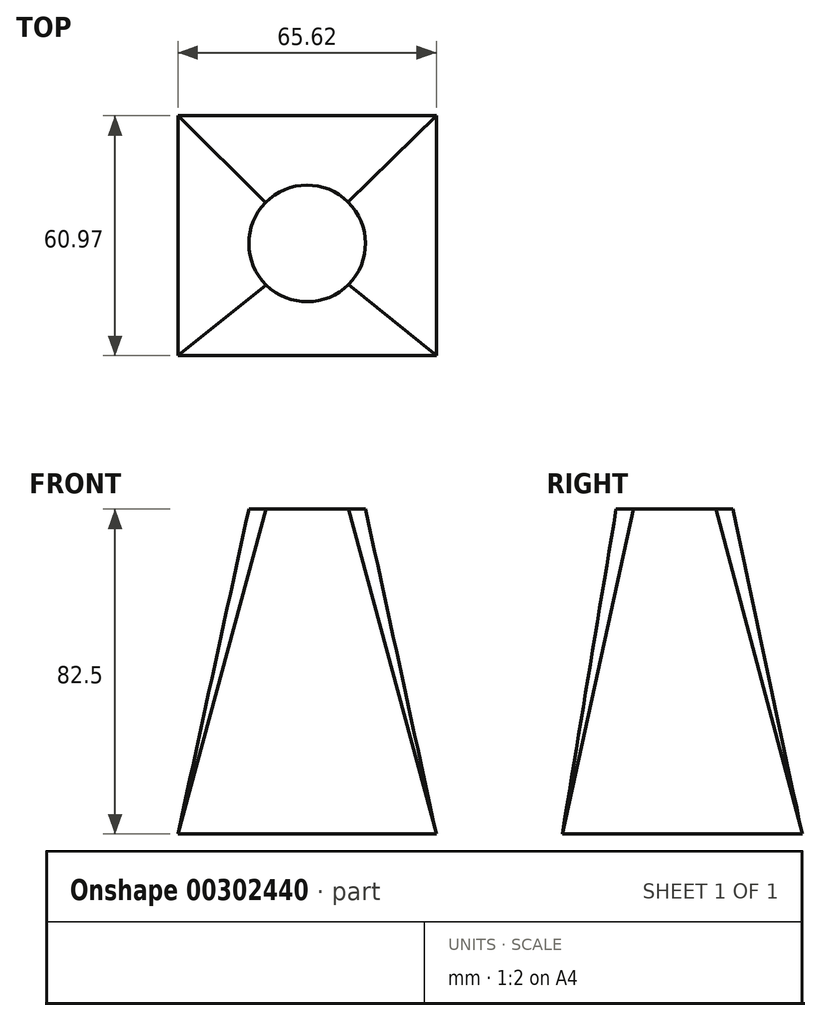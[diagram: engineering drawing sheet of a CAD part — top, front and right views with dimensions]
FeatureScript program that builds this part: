
annotation { "Feature Type Name" : "Feature", "Feature Type Description" : "" }
export const myFeature = defineFeature(function(context is Context, id is Id, definition is map)
    precondition{}
    {
        {
            var Q0;
            Q0=qCreatedBy(makeId("Top.planeOp"),FACE);
            var sketch = newSketch(context, id + "F0", { "sketchPlane" : qUnion([Q0])});
            skLineSegment(sketch, "E0.bottom", {"start": v(-32.81, 32.47) * mm, "end": v(32.81, 32.47) * mm});
            skLineSegment(sketch, "E0.top", {"start": v(-32.81, -28.5) * mm, "end": v(32.81, -28.5) * mm});
            skLineSegment(sketch, "E0.left", {"start": v(-32.81, 32.47) * mm, "end": v(-32.81, -28.5) * mm});
            skLineSegment(sketch, "E0.right", {"start": v(32.81, 32.47) * mm, "end": v(32.81, -28.5) * mm});
            skSolve(sketch);
        }
        {
            var Q0;
            Q0=makeQuery(id+"F0.imprint","IMPRINT",FACE,{"disambiguationData":[TD([[makeQuery(id+"F0.imprint","IMPRINT",EDGE,{"derivedFrom":sQuery(id+"F0.wireOp",EDGE,"E0.bottom")}),-1.0]])]});
            cPlane(context, id + "F1", {"entities" : qUnion([Q0]), "cplaneType" : CPlaneType.OFFSET, "offset" : 82.5 * mm, "width" : 150 * mm, "height" : 150 * mm});
        }
        {
            var Q0;
            Q0=qCreatedBy(id+"F1.planeOp",FACE);
            var sketch = newSketch(context, id + "F2", { "sketchPlane" : qUnion([Q0])});
            skCircle(sketch, "E1", {"center": v(0, 0) * mm, "radius": 14.82 * mm});
            skSolve(sketch);
        }
        {
            var Q0;
            Q0=makeQuery(id+"F0.imprint","IMPRINT",FACE,{"disambiguationData":[TD([[makeQuery(id+"F0.imprint","IMPRINT",EDGE,{"derivedFrom":sQuery(id+"F0.wireOp",EDGE,"E0.bottom")}),-1.0]])]});
            var Q1;
            Q1=makeQuery(id+"F2.imprint","IMPRINT",FACE,{"disambiguationData":[TD([[makeQuery(id+"F2.imprint","IMPRINT",EDGE,{"derivedFrom":sQuery(id+"F2.wireOp",EDGE,"E1")}),1.0]])]});
            loft(context, id + "F3", {"sheetProfilesArray" : [{ "sheetProfileEntities" : qUnion([Q0]) }, { "sheetProfileEntities" : qUnion([Q1]) }]});
        }
    });
